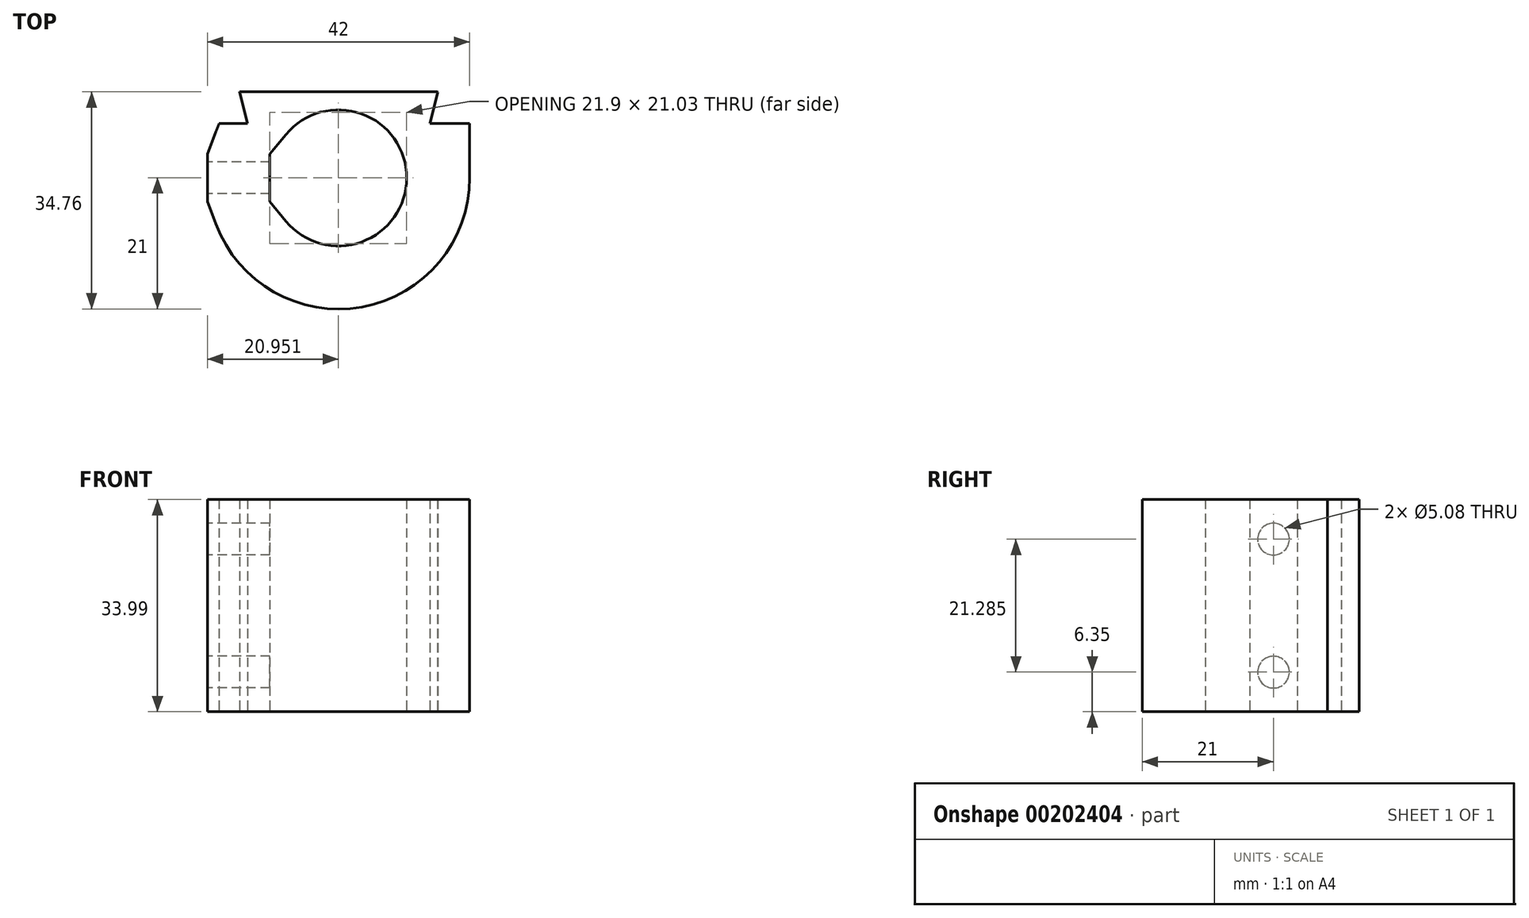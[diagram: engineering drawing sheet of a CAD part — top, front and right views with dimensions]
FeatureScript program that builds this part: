
annotation { "Feature Type Name" : "Feature", "Feature Type Description" : "" }
export const myFeature = defineFeature(function(context is Context, id is Id, definition is map)
    precondition{}
    {
        {
            var Q0;
            Q0=qCreatedBy(makeId("Top.planeOp"),FACE);
            var sketch = newSketch(context, id + "F0", { "sketchPlane" : qUnion([Q0])});
            skArc(sketch, "E0", {"start": v(-8.4, -6.95) * mm, "mid": v(10.9, 0) * mm, "end": v(-8.4, 6.95) * mm});
            skArc(sketch, "E1", {"start": v(-19.66, -7.38) * mm, "mid": v(3.75, -20.66) * mm, "end": v(21, 0) * mm});
            skLineSegment(sketch, "E2", {"start": v(-11, 3.81) * mm, "end": v(-11, -3.81) * mm});
            skLineSegment(sketch, "E3", {"start": v(-15.87, 13.76) * mm, "end": v(15.88, 13.76) * mm});
            skLineSegment(sketch, "E4", {"start": v(-15.88, 13.76) * mm, "end": v(-14.6, 8.68) * mm});
            skLineSegment(sketch, "E5", {"start": v(-14.6, 8.68) * mm, "end": v(-19.12, 8.68) * mm});
            skLineSegment(sketch, "E6", {"start": v(15.88, 13.76) * mm, "end": v(14.6, 8.68) * mm});
            skLineSegment(sketch, "E7", {"start": v(14.6, 8.68) * mm, "end": v(19.12, 8.68) * mm});
            skPoint(sketch, "E8", {"position": v(-11, 0) * mm});
            skLineSegment(sketch, "E9", {"start": v(-11, 3.81) * mm, "end": v(-8.4, 6.95) * mm});
            skLineSegment(sketch, "E10", {"start": v(-11, -3.81) * mm, "end": v(-8.4, -6.95) * mm});
            skLineSegment(sketch, "E11", {"start": v(-21, 3.81) * mm, "end": v(-21, -3.81) * mm});
            skPoint(sketch, "E12", {"position": v(-21, 0) * mm});
            skLineSegment(sketch, "E13", {"start": v(-21, 3.8) * mm, "end": v(-19.66, 7.38) * mm});
            skLineSegment(sketch, "E14", {"start": v(-21, -3.81) * mm, "end": v(-19.66, -7.38) * mm});
            skPoint(sketch, "E15", {"position": v(0, 13.76) * mm});
            skArc(sketch, "E16.trimOffspring", {"start": v(-19.12, 8.68) * mm, "mid": v(-19.4, 8.03) * mm, "end": v(-19.66, 7.38) * mm});
            skArc(sketch, "E17.trimOffspring", {"start": v(-15.87, 13.76) * mm, "mid": v(-15.87, 13.75) * mm, "end": v(-15.87, 13.75) * mm});
            skLineSegment(sketch, "E18", {"start": v(21, 8.68) * mm, "end": v(21, 0) * mm});
            skLineSegment(sketch, "E19", {"start": v(19.12, 8.68) * mm, "end": v(21, 8.68) * mm});
            skArc(sketch, "E20.trimOffspring", {"start": v(15.87, 13.75) * mm, "mid": v(15.87, 13.75) * mm, "end": v(15.87, 13.76) * mm});
            skSolve(sketch);
        }
        {
            var Q0;
            Q0=makeQuery(id+"F0.imprint","IMPRINT",FACE,{"disambiguationData":[TD([[makeQuery(id+"F0.imprint","IMPRINT",EDGE,{"derivedFrom":sQuery(id+"F0.wireOp",EDGE,"E0")}),-1.0]])]});
            extrude(context, id + "F1", {"entities" : qUnion([Q0]), "depth" : 34 * mm});
        }
        {
            var Q0;
            Q0=makeQuery(id+"F1.opExtrude","SWEPT_FACE",FACE,{"disambiguationData":[OSD([sQuery(id+"F0.wireOp",EDGE,"E11")])]});
            var sketch = newSketch(context, id + "F2", { "sketchPlane" : qUnion([Q0])});
            skCircle(sketch, "E21", {"center": v(0, 6.35) * mm, "radius": 2.54 * mm});
            skCircle(sketch, "E22", {"center": v(0, 27.64) * mm, "radius": 2.54 * mm});
            skSolve(sketch);
        }
        {
            var Q0;
            Q0=makeQuery(id+"F2.imprint","IMPRINT",FACE,{"disambiguationData":[TD([[makeQuery(id+"F2.imprint","IMPRINT",EDGE,{"derivedFrom":sQuery(id+"F2.wireOp",EDGE,"E21")}),1.0]])]});
            var Q1;
            Q1=makeQuery(id+"F2.imprint","IMPRINT",FACE,{"disambiguationData":[TD([[makeQuery(id+"F2.imprint","IMPRINT",EDGE,{"derivedFrom":sQuery(id+"F2.wireOp",EDGE,"E22")}),1.0]])]});
            extrude(context, id + "F3", {"entities" : qUnion([Q0, Q1]), "operationType" : NewBodyOperationType.REMOVE, "endBound" : BoundingType.UP_TO_NEXT, "oppositeDirection" : true, "depth" : 25.4 * mm});
        }
    });
